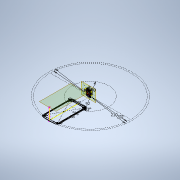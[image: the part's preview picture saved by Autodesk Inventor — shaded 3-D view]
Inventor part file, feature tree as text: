
AUTODESK INVENTOR PART (.ipt)
format: ipt  version: 2020 (Build 240168000, 168)  size: 652,800 bytes
history: native  units: mm
features: projected_geometry x31, extrude x19, sketch x13, fillet x10, other x7, chamfer x2
ambient origin geometry x8: Origin, YZ Plane, XZ Plane, XY Plane, X Axis, Y Axis, Z Axis, Center Point
bodies: Body1 (feature_tree)
feature tree (82):
  other  "Твердое тело1"
  sketch  "Эскиз1"
  extrude  "Выдавливание3"  Depth=202.0mm
  other  "РабПлоскость1"
  extrude  "Выдавливание1"  Depth=35.0mm
  other  "РабПлоскость2"
  sketch  "Эскиз2"
  extrude  "Выдавливание4"  Depth=68.0mm
  extrude  "Выдавливание5"  Depth=2.0mm
  sketch  "Эскиз4"
  extrude  "Выдавливание6"  Depth=2.0mm
  extrude  "Выдавливание7"  Depth=3.0mm
  other  "РабПлоскость3"
  extrude  "Выдавливание8"  Depth=3.0mm
  other  "РабПлоскость4"
  extrude  "Выдавливание9"  Depth=210.0mm
  sketch  "Эскиз8"
  extrude  "Выдавливание10"  Depth=20.0mm TaperAngle=0.0deg
  fillet  "Сопряжение1"  Radius=1.5mm
  fillet  "Сопряжение2"  Radius=28.0mm
  fillet  "Сопряжение3"  Radius=7.0mm
  fillet  "Сопряжение4"  Radius=20.0mm
  fillet  "Сопряжение5"  Radius=13.0mm
  extrude  "Выдавливание11"  Depth=5.0mm
  extrude  "Выдавливание12"  Depth=3.0mm
  fillet  "Сопряжение6"  Radius=10.0mm
  extrude  "Выдавливание13"  Depth=84.0mm
  chamfer  "Фаска1"  Distance=5.0mm
  fillet  "Сопряжение7"  Radius=52.0mm
  sketch  "Эскиз10"
  other  "РабПлоскость5"
  extrude  "Выдавливание14"  Depth=5.0mm TaperAngle=0.0deg
  fillet  "Сопряжение8"  Radius=35.0mm
  extrude  "Выдавливание15"  Depth=18.0mm
  fillet  "Сопряжение9"  Radius=3.0mm
  extrude  "Выдавливание16"  Depth=30.0mm TaperAngle=360.0deg
  fillet  "Сопряжение10"  Radius=0.5mm
  extrude  "Выдавливание17"  TaperAngle=0.0deg  [1 undecoded]
  chamfer  "Фаска2"  Distance=8.0mm
  other  "РабПлоскость7"
  sketch  "Эскиз13"
  extrude  "Выдавливание18"  Depth=2.0mm
  extrude  "Выдавливание19"  Depth=1.5mm TaperAngle=0.0deg
  extrude  "Выдавливание20"  Depth=2.0mm
  projected_geometry  "Спроецированная петля1"
  projected_geometry  "Спроецированная петля7"
  projected_geometry  "Спроецированная петля8"
  sketch  "Эскиз3"
  projected_geometry  "Спроецированная петля9"
  projected_geometry  "Спроецированная петля10"
  projected_geometry  "Спроецированная петля11"
  projected_geometry  "Спроецированная петля12"
  sketch  "Эскиз5"
  projected_geometry  "Спроецированная петля13"
  projected_geometry  "Спроецированная петля14"
  projected_geometry  "Спроецированная петля15"
  projected_geometry  "Спроецированная петля16"
  projected_geometry  "Спроецированная петля17"
  sketch  "Эскиз6"
  projected_geometry  "Спроецированная петля18"
  projected_geometry  "Спроецированная петля19"
  projected_geometry  "Спроецированная петля20"
  projected_geometry  "Спроецированная петля21"
  projected_geometry  "Спроецированная петля22"
  projected_geometry  "Спроецированная петля23"
  projected_geometry  "Спроецированная петля24"
  projected_geometry  "Спроецированная петля25"
  projected_geometry  "Спроецированная петля26"
  projected_geometry  "Спроецированная петля27"
  projected_geometry  "Спроецированная петля28"
  sketch  "Эскиз9"
  projected_geometry  "Спроецированная петля29"
  projected_geometry  "Спроецированная петля30"
  sketch  "Эскиз11"
  projected_geometry  "Спроецированная петля31"
  projected_geometry  "Спроецированная петля32"
  projected_geometry  "Спроецированная петля33"
  sketch  "Эскиз12"
  projected_geometry  "Спроецированная петля34"
  projected_geometry  "Спроецированная петля35"
  projected_geometry  "Спроецированная петля36"
  sketch  "Эскиз14"
note: 1 required parameter value undecoded (feature->parameter linkage not recoverable at this tier; creation-order binding heuristic only, values carry confidence <= 0.55)
